# Revit family: FONESTAR_Proyector_Sonido_Exterior_EN-54
name_source: partatom
category: Communication Devices
units: mm (PartAtom-declared; Revit-internal decimal feet)

## family parameters
Always vertical = No
Cut with Voids When Loaded = No
Maintain Annotation Orientation = No
Part Type = Normal
Room Calculation Point = No
Round Connector Dimension = Use Diameter
Shared = No
Work Plane-Based = Yes

## types (1)
- PF-31T-EN
    Altura = 215 mm  [stored 0.705381 ft]
    Cuerpo.Espesor = 5 mm  [stored 0.0164042 ft]
    Cuerpo.Material = Plástico ABS - Gris RAL(7035)
    Default Elevation = 1000 mm  [stored 3.28084 ft]
    Description = Proyector de sonido con difusor EN 54, transformador de línea de 100 V y carcasa antifuego.
    Longitud = 315 mm  [stored 1.03346 ft]
    Manufacturer = FONESTAR
    Model = PF-31T-EN
    Modified by = XPV
    Peso = 5 Kg
    Potencia Acústica = 30 W RMS
    Profundidad = 355 mm  [stored 1.1647 ft]
    Protección IP = IP-66
    Respuesta Acústica = 130-20000 Hz
    Reviewed by = TAG
    Soporte.Altura = 235 mm  [stored 0.770997 ft]
    Soporte.Anchura = 40 mm  [stored 0.131234 ft]
    Soporte.Espesor = 3 mm  [stored 0.00984252 ft]
    Soporte.Longitud = 275 mm
    Soporte.Material = Plástico ABS - Gris RAL(7035)
    URL = https://fonestar.com
    URL.Product = https://fonestar.com
    Version = R1

note: [stored X ft] marks values corroborated as IEEE doubles in the binary element streams (Revit-internal decimal feet)
